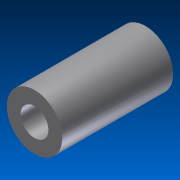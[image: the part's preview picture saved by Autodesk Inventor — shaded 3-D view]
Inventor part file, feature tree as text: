
AUTODESK INVENTOR PART (.ipt)
format: ipt  version: 2012 (Build 160160000, 160)  size: 81,408 bytes
history: native  units: in
note: dims shown in document units (in); Inventor stores cm internally (conversion verified against a paired STEP export)
features: extrude x1, sketch x1
ambient origin geometry x8: Origin, YZ Plane, XZ Plane, XY Plane, X Axis, Y Axis, Z Axis, Center Point
bodies: Solid1 (feature_tree)
feature tree (2):
  extrude  "Extrusion1"  Depth=0.2362in
  sketch  "Sketch1"  dims[d0=0.1181in d1=0.2362in d2=0.4724in d3=0.0in]
